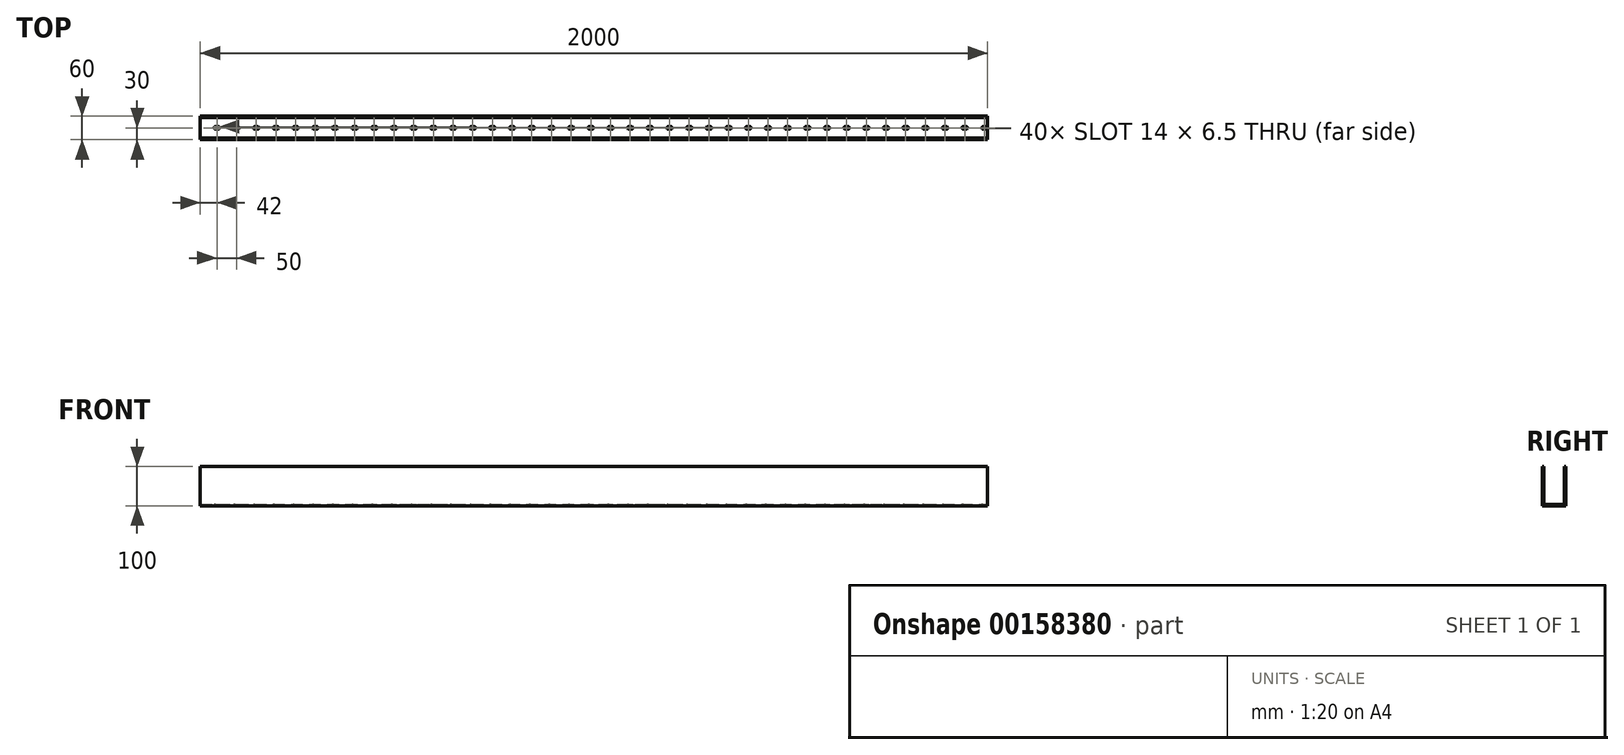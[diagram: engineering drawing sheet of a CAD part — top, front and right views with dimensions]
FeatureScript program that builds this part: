
annotation { "Feature Type Name" : "Feature", "Feature Type Description" : "" }
export const myFeature = defineFeature(function(context is Context, id is Id, definition is map)
    precondition{}
    {
        {
            var Q0;
            Q0=qCreatedBy(makeId("Top.planeOp"),FACE);
            var sketch = newSketch(context, id + "F0", { "sketchPlane" : qUnion([Q0])});
            skLineSegment(sketch, "E0.bottom", {"start": v(0, 0) * mm, "end": v(2000, 0) * mm});
            skLineSegment(sketch, "E0.top", {"start": v(0, 60) * mm, "end": v(2000, 60) * mm});
            skLineSegment(sketch, "E0.left", {"start": v(0, 0) * mm, "end": v(0, 60) * mm});
            skLineSegment(sketch, "E0.right", {"start": v(2000, 0) * mm, "end": v(2000, 60) * mm});
            skSolve(sketch);
        }
        {
            var Q0;
            Q0=qSketchRegion(id+"F0",true);
            extrude(context, id + "F1", {"entities" : qUnion([Q0]), "depth" : 100 * mm});
        }
        {
            var Q0;
            Q0=makeQuery(id+"F1.opExtrude","CAP_FACE",FACE,{"disambiguationData":[OSD([sQuery(id+"F0.wireOp",EDGE,"E0.bottom"),sQuery(id+"F0.wireOp",EDGE,"E0.top"),sQuery(id+"F0.wireOp",EDGE,"E0.left"),sQuery(id+"F0.wireOp",EDGE,"E0.right")])],"isStart":false});
            var sketch = newSketch(context, id + "F2", { "sketchPlane" : qUnion([Q0])});
            skLineSegment(sketch, "E1.bottom", {"start": v(0, 56) * mm, "end": v(2000, 56) * mm});
            skLineSegment(sketch, "E1.top", {"start": v(0, 4) * mm, "end": v(2000, 4) * mm});
            skLineSegment(sketch, "E1.left", {"start": v(0, 56) * mm, "end": v(0, 4) * mm});
            skLineSegment(sketch, "E1.right", {"start": v(2000, 56) * mm, "end": v(2000, 4) * mm});
            skSolve(sketch);
        }
        {
            var Q0;
            Q0=qSketchRegion(id+"F2",true);
            extrude(context, id + "F3", {"entities" : qUnion([Q0]), "operationType" : NewBodyOperationType.REMOVE, "oppositeDirection" : true, "depth" : (100 - 4) * mm});
        }
        {
            var Q0;
            Q0=makeQuery(id+"F3.boolean.opBoolean","COPY",FACE,{"derivedFrom":makeQuery(id+"F3.opExtrude","CAP_FACE",FACE,{"disambiguationData":[OSD([sQuery(id+"F2.wireOp",EDGE,"E1.bottom"),sQuery(id+"F2.wireOp",EDGE,"E1.top"),sQuery(id+"F2.wireOp",EDGE,"E1.left"),sQuery(id+"F2.wireOp",EDGE,"E1.right")])],"isStart":false})});
            var sketch = newSketch(context, id + "F4", { "sketchPlane" : qUnion([Q0])});
            skLineSegment(sketch, "E2", {"start": v(38.25, 30) * mm, "end": v(45.75, 30) * mm, "construction": true});
            skArc(sketch, "E3.0.startCap", {"start": v(38.25, 26.75) * mm, "mid": v(35, 30) * mm, "end": v(38.25, 33.25) * mm});
            skArc(sketch, "E3.0.endCap", {"start": v(45.75, 33.25) * mm, "mid": v(49, 30) * mm, "end": v(45.75, 26.75) * mm});
            skLineSegment(sketch, "E3.0.left", {"start": v(38.25, 33.25) * mm, "end": v(45.75, 33.25) * mm});
            skLineSegment(sketch, "E3.0.right", {"start": v(38.25, 26.75) * mm, "end": v(45.75, 26.75) * mm});
            skLineSegment(sketch, "E4.1.0.0", {"start": v(88.25, 26.75) * mm, "end": v(95.75, 26.75) * mm});
            skArc(sketch, "E4.1.0.1", {"start": v(88.25, 26.75) * mm, "mid": v(85, 30) * mm, "end": v(88.25, 33.25) * mm});
            skLineSegment(sketch, "E4.1.0.2", {"start": v(88.25, 33.25) * mm, "end": v(95.75, 33.25) * mm});
            skArc(sketch, "E4.1.0.3", {"start": v(95.75, 33.25) * mm, "mid": v(99, 30) * mm, "end": v(95.75, 26.75) * mm});
            skLineSegment(sketch, "E4.2.0.0", {"start": v(138.25, 26.75) * mm, "end": v(145.75, 26.75) * mm});
            skArc(sketch, "E4.2.0.1", {"start": v(138.25, 26.75) * mm, "mid": v(135, 30) * mm, "end": v(138.25, 33.25) * mm});
            skLineSegment(sketch, "E4.2.0.2", {"start": v(138.25, 33.25) * mm, "end": v(145.75, 33.25) * mm});
            skArc(sketch, "E4.2.0.3", {"start": v(145.75, 33.25) * mm, "mid": v(149, 30) * mm, "end": v(145.75, 26.75) * mm});
            skLineSegment(sketch, "E4.3.0.0", {"start": v(188.25, 26.75) * mm, "end": v(195.75, 26.75) * mm});
            skArc(sketch, "E4.3.0.1", {"start": v(188.25, 26.75) * mm, "mid": v(185, 30) * mm, "end": v(188.25, 33.25) * mm});
            skLineSegment(sketch, "E4.3.0.2", {"start": v(188.25, 33.25) * mm, "end": v(195.75, 33.25) * mm});
            skArc(sketch, "E4.3.0.3", {"start": v(195.75, 33.25) * mm, "mid": v(199, 30) * mm, "end": v(195.75, 26.75) * mm});
            skLineSegment(sketch, "E4.4.0.0", {"start": v(238.25, 26.75) * mm, "end": v(245.75, 26.75) * mm});
            skArc(sketch, "E4.4.0.1", {"start": v(238.25, 26.75) * mm, "mid": v(235, 30) * mm, "end": v(238.25, 33.25) * mm});
            skLineSegment(sketch, "E4.4.0.2", {"start": v(238.25, 33.25) * mm, "end": v(245.75, 33.25) * mm});
            skArc(sketch, "E4.4.0.3", {"start": v(245.75, 33.25) * mm, "mid": v(249, 30) * mm, "end": v(245.75, 26.75) * mm});
            skLineSegment(sketch, "E4.5.0.0", {"start": v(288.25, 26.75) * mm, "end": v(295.75, 26.75) * mm});
            skArc(sketch, "E4.5.0.1", {"start": v(288.25, 26.75) * mm, "mid": v(285, 30) * mm, "end": v(288.25, 33.25) * mm});
            skLineSegment(sketch, "E4.5.0.2", {"start": v(288.25, 33.25) * mm, "end": v(295.75, 33.25) * mm});
            skArc(sketch, "E4.5.0.3", {"start": v(295.75, 33.25) * mm, "mid": v(299, 30) * mm, "end": v(295.75, 26.75) * mm});
            skLineSegment(sketch, "E4.6.0.0", {"start": v(338.25, 26.75) * mm, "end": v(345.75, 26.75) * mm});
            skArc(sketch, "E4.6.0.1", {"start": v(338.25, 26.75) * mm, "mid": v(335, 30) * mm, "end": v(338.25, 33.25) * mm});
            skLineSegment(sketch, "E4.6.0.2", {"start": v(338.25, 33.25) * mm, "end": v(345.75, 33.25) * mm});
            skArc(sketch, "E4.6.0.3", {"start": v(345.75, 33.25) * mm, "mid": v(349, 30) * mm, "end": v(345.75, 26.75) * mm});
            skLineSegment(sketch, "E4.7.0.0", {"start": v(388.25, 26.75) * mm, "end": v(395.75, 26.75) * mm});
            skArc(sketch, "E4.7.0.1", {"start": v(388.25, 26.75) * mm, "mid": v(385, 30) * mm, "end": v(388.25, 33.25) * mm});
            skLineSegment(sketch, "E4.7.0.2", {"start": v(388.25, 33.25) * mm, "end": v(395.75, 33.25) * mm});
            skArc(sketch, "E4.7.0.3", {"start": v(395.75, 33.25) * mm, "mid": v(399, 30) * mm, "end": v(395.75, 26.75) * mm});
            skLineSegment(sketch, "E4.8.0.0", {"start": v(438.25, 26.75) * mm, "end": v(445.75, 26.75) * mm});
            skArc(sketch, "E4.8.0.1", {"start": v(438.25, 26.75) * mm, "mid": v(435, 30) * mm, "end": v(438.25, 33.25) * mm});
            skLineSegment(sketch, "E4.8.0.2", {"start": v(438.25, 33.25) * mm, "end": v(445.75, 33.25) * mm});
            skArc(sketch, "E4.8.0.3", {"start": v(445.75, 33.25) * mm, "mid": v(449, 30) * mm, "end": v(445.75, 26.75) * mm});
            skLineSegment(sketch, "E4.9.0.0", {"start": v(488.25, 26.75) * mm, "end": v(495.75, 26.75) * mm});
            skArc(sketch, "E4.9.0.1", {"start": v(488.25, 26.75) * mm, "mid": v(485, 30) * mm, "end": v(488.25, 33.25) * mm});
            skLineSegment(sketch, "E4.9.0.2", {"start": v(488.25, 33.25) * mm, "end": v(495.75, 33.25) * mm});
            skArc(sketch, "E4.9.0.3", {"start": v(495.75, 33.25) * mm, "mid": v(499, 30) * mm, "end": v(495.75, 26.75) * mm});
            skLineSegment(sketch, "E4.10.0.0", {"start": v(538.25, 26.75) * mm, "end": v(545.75, 26.75) * mm});
            skArc(sketch, "E4.10.0.1", {"start": v(538.25, 26.75) * mm, "mid": v(535, 30) * mm, "end": v(538.25, 33.25) * mm});
            skLineSegment(sketch, "E4.10.0.2", {"start": v(538.25, 33.25) * mm, "end": v(545.75, 33.25) * mm});
            skArc(sketch, "E4.10.0.3", {"start": v(545.75, 33.25) * mm, "mid": v(549, 30) * mm, "end": v(545.75, 26.75) * mm});
            skLineSegment(sketch, "E4.11.0.0", {"start": v(588.25, 26.75) * mm, "end": v(595.75, 26.75) * mm});
            skArc(sketch, "E4.11.0.1", {"start": v(588.25, 26.75) * mm, "mid": v(585, 30) * mm, "end": v(588.25, 33.25) * mm});
            skLineSegment(sketch, "E4.11.0.2", {"start": v(588.25, 33.25) * mm, "end": v(595.75, 33.25) * mm});
            skArc(sketch, "E4.11.0.3", {"start": v(595.75, 33.25) * mm, "mid": v(599, 30) * mm, "end": v(595.75, 26.75) * mm});
            skLineSegment(sketch, "E4.12.0.0", {"start": v(638.25, 26.75) * mm, "end": v(645.75, 26.75) * mm});
            skArc(sketch, "E4.12.0.1", {"start": v(638.25, 26.75) * mm, "mid": v(635, 30) * mm, "end": v(638.25, 33.25) * mm});
            skLineSegment(sketch, "E4.12.0.2", {"start": v(638.25, 33.25) * mm, "end": v(645.75, 33.25) * mm});
            skArc(sketch, "E4.12.0.3", {"start": v(645.75, 33.25) * mm, "mid": v(649, 30) * mm, "end": v(645.75, 26.75) * mm});
            skLineSegment(sketch, "E4.13.0.0", {"start": v(688.25, 26.75) * mm, "end": v(695.75, 26.75) * mm});
            skArc(sketch, "E4.13.0.1", {"start": v(688.25, 26.75) * mm, "mid": v(685, 30) * mm, "end": v(688.25, 33.25) * mm});
            skLineSegment(sketch, "E4.13.0.2", {"start": v(688.25, 33.25) * mm, "end": v(695.75, 33.25) * mm});
            skArc(sketch, "E4.13.0.3", {"start": v(695.75, 33.25) * mm, "mid": v(699, 30) * mm, "end": v(695.75, 26.75) * mm});
            skLineSegment(sketch, "E4.14.0.0", {"start": v(738.25, 26.75) * mm, "end": v(745.75, 26.75) * mm});
            skArc(sketch, "E4.14.0.1", {"start": v(738.25, 26.75) * mm, "mid": v(735, 30) * mm, "end": v(738.25, 33.25) * mm});
            skLineSegment(sketch, "E4.14.0.2", {"start": v(738.25, 33.25) * mm, "end": v(745.75, 33.25) * mm});
            skArc(sketch, "E4.14.0.3", {"start": v(745.75, 33.25) * mm, "mid": v(749, 30) * mm, "end": v(745.75, 26.75) * mm});
            skLineSegment(sketch, "E4.15.0.0", {"start": v(788.25, 26.75) * mm, "end": v(795.75, 26.75) * mm});
            skArc(sketch, "E4.15.0.1", {"start": v(788.25, 26.75) * mm, "mid": v(785, 30) * mm, "end": v(788.25, 33.25) * mm});
            skLineSegment(sketch, "E4.15.0.2", {"start": v(788.25, 33.25) * mm, "end": v(795.75, 33.25) * mm});
            skArc(sketch, "E4.15.0.3", {"start": v(795.75, 33.25) * mm, "mid": v(799, 30) * mm, "end": v(795.75, 26.75) * mm});
            skLineSegment(sketch, "E4.16.0.0", {"start": v(838.25, 26.75) * mm, "end": v(845.75, 26.75) * mm});
            skArc(sketch, "E4.16.0.1", {"start": v(838.25, 26.75) * mm, "mid": v(835, 30) * mm, "end": v(838.25, 33.25) * mm});
            skLineSegment(sketch, "E4.16.0.2", {"start": v(838.25, 33.25) * mm, "end": v(845.75, 33.25) * mm});
            skArc(sketch, "E4.16.0.3", {"start": v(845.75, 33.25) * mm, "mid": v(849, 30) * mm, "end": v(845.75, 26.75) * mm});
            skLineSegment(sketch, "E4.17.0.0", {"start": v(888.25, 26.75) * mm, "end": v(895.75, 26.75) * mm});
            skArc(sketch, "E4.17.0.1", {"start": v(888.25, 26.75) * mm, "mid": v(885, 30) * mm, "end": v(888.25, 33.25) * mm});
            skLineSegment(sketch, "E4.17.0.2", {"start": v(888.25, 33.25) * mm, "end": v(895.75, 33.25) * mm});
            skArc(sketch, "E4.17.0.3", {"start": v(895.75, 33.25) * mm, "mid": v(899, 30) * mm, "end": v(895.75, 26.75) * mm});
            skLineSegment(sketch, "E4.18.0.0", {"start": v(938.25, 26.75) * mm, "end": v(945.75, 26.75) * mm});
            skArc(sketch, "E4.18.0.1", {"start": v(938.25, 26.75) * mm, "mid": v(935, 30) * mm, "end": v(938.25, 33.25) * mm});
            skLineSegment(sketch, "E4.18.0.2", {"start": v(938.25, 33.25) * mm, "end": v(945.75, 33.25) * mm});
            skArc(sketch, "E4.18.0.3", {"start": v(945.75, 33.25) * mm, "mid": v(949, 30) * mm, "end": v(945.75, 26.75) * mm});
            skLineSegment(sketch, "E4.19.0.0", {"start": v(988.25, 26.75) * mm, "end": v(995.75, 26.75) * mm});
            skArc(sketch, "E4.19.0.1", {"start": v(988.25, 26.75) * mm, "mid": v(985, 30) * mm, "end": v(988.25, 33.25) * mm});
            skLineSegment(sketch, "E4.19.0.2", {"start": v(988.25, 33.25) * mm, "end": v(995.75, 33.25) * mm});
            skArc(sketch, "E4.19.0.3", {"start": v(995.75, 33.25) * mm, "mid": v(999, 30) * mm, "end": v(995.75, 26.75) * mm});
            skLineSegment(sketch, "E4.20.0.0", {"start": v(1038.25, 26.75) * mm, "end": v(1045.75, 26.75) * mm});
            skArc(sketch, "E4.20.0.1", {"start": v(1038.25, 26.75) * mm, "mid": v(1035, 30) * mm, "end": v(1038.25, 33.25) * mm});
            skLineSegment(sketch, "E4.20.0.2", {"start": v(1038.25, 33.25) * mm, "end": v(1045.75, 33.25) * mm});
            skArc(sketch, "E4.20.0.3", {"start": v(1045.75, 33.25) * mm, "mid": v(1049, 30) * mm, "end": v(1045.75, 26.75) * mm});
            skLineSegment(sketch, "E4.21.0.0", {"start": v(1088.25, 26.75) * mm, "end": v(1095.75, 26.75) * mm});
            skArc(sketch, "E4.21.0.1", {"start": v(1088.25, 26.75) * mm, "mid": v(1085, 30) * mm, "end": v(1088.25, 33.25) * mm});
            skLineSegment(sketch, "E4.21.0.2", {"start": v(1088.25, 33.25) * mm, "end": v(1095.75, 33.25) * mm});
            skArc(sketch, "E4.21.0.3", {"start": v(1095.75, 33.25) * mm, "mid": v(1099, 30) * mm, "end": v(1095.75, 26.75) * mm});
            skLineSegment(sketch, "E4.22.0.0", {"start": v(1138.25, 26.75) * mm, "end": v(1145.75, 26.75) * mm});
            skArc(sketch, "E4.22.0.1", {"start": v(1138.25, 26.75) * mm, "mid": v(1135, 30) * mm, "end": v(1138.25, 33.25) * mm});
            skLineSegment(sketch, "E4.22.0.2", {"start": v(1138.25, 33.25) * mm, "end": v(1145.75, 33.25) * mm});
            skArc(sketch, "E4.22.0.3", {"start": v(1145.75, 33.25) * mm, "mid": v(1149, 30) * mm, "end": v(1145.75, 26.75) * mm});
            skLineSegment(sketch, "E4.23.0.0", {"start": v(1188.25, 26.75) * mm, "end": v(1195.75, 26.75) * mm});
            skArc(sketch, "E4.23.0.1", {"start": v(1188.25, 26.75) * mm, "mid": v(1185, 30) * mm, "end": v(1188.25, 33.25) * mm});
            skLineSegment(sketch, "E4.23.0.2", {"start": v(1188.25, 33.25) * mm, "end": v(1195.75, 33.25) * mm});
            skArc(sketch, "E4.23.0.3", {"start": v(1195.75, 33.25) * mm, "mid": v(1199, 30) * mm, "end": v(1195.75, 26.75) * mm});
            skLineSegment(sketch, "E4.24.0.0", {"start": v(1238.25, 26.75) * mm, "end": v(1245.75, 26.75) * mm});
            skArc(sketch, "E4.24.0.1", {"start": v(1238.25, 26.75) * mm, "mid": v(1235, 30) * mm, "end": v(1238.25, 33.25) * mm});
            skLineSegment(sketch, "E4.24.0.2", {"start": v(1238.25, 33.25) * mm, "end": v(1245.75, 33.25) * mm});
            skArc(sketch, "E4.24.0.3", {"start": v(1245.75, 33.25) * mm, "mid": v(1249, 30) * mm, "end": v(1245.75, 26.75) * mm});
            skLineSegment(sketch, "E4.25.0.0", {"start": v(1288.25, 26.75) * mm, "end": v(1295.75, 26.75) * mm});
            skArc(sketch, "E4.25.0.1", {"start": v(1288.25, 26.75) * mm, "mid": v(1285, 30) * mm, "end": v(1288.25, 33.25) * mm});
            skLineSegment(sketch, "E4.25.0.2", {"start": v(1288.25, 33.25) * mm, "end": v(1295.75, 33.25) * mm});
            skArc(sketch, "E4.25.0.3", {"start": v(1295.75, 33.25) * mm, "mid": v(1299, 30) * mm, "end": v(1295.75, 26.75) * mm});
            skLineSegment(sketch, "E4.26.0.0", {"start": v(1338.25, 26.75) * mm, "end": v(1345.75, 26.75) * mm});
            skArc(sketch, "E4.26.0.1", {"start": v(1338.25, 26.75) * mm, "mid": v(1335, 30) * mm, "end": v(1338.25, 33.25) * mm});
            skLineSegment(sketch, "E4.26.0.2", {"start": v(1338.25, 33.25) * mm, "end": v(1345.75, 33.25) * mm});
            skArc(sketch, "E4.26.0.3", {"start": v(1345.75, 33.25) * mm, "mid": v(1349, 30) * mm, "end": v(1345.75, 26.75) * mm});
            skLineSegment(sketch, "E4.27.0.0", {"start": v(1388.25, 26.75) * mm, "end": v(1395.75, 26.75) * mm});
            skArc(sketch, "E4.27.0.1", {"start": v(1388.25, 26.75) * mm, "mid": v(1385, 30) * mm, "end": v(1388.25, 33.25) * mm});
            skLineSegment(sketch, "E4.27.0.2", {"start": v(1388.25, 33.25) * mm, "end": v(1395.75, 33.25) * mm});
            skArc(sketch, "E4.27.0.3", {"start": v(1395.75, 33.25) * mm, "mid": v(1399, 30) * mm, "end": v(1395.75, 26.75) * mm});
            skLineSegment(sketch, "E4.28.0.0", {"start": v(1438.25, 26.75) * mm, "end": v(1445.75, 26.75) * mm});
            skArc(sketch, "E4.28.0.1", {"start": v(1438.25, 26.75) * mm, "mid": v(1435, 30) * mm, "end": v(1438.25, 33.25) * mm});
            skLineSegment(sketch, "E4.28.0.2", {"start": v(1438.25, 33.25) * mm, "end": v(1445.75, 33.25) * mm});
            skArc(sketch, "E4.28.0.3", {"start": v(1445.75, 33.25) * mm, "mid": v(1449, 30) * mm, "end": v(1445.75, 26.75) * mm});
            skLineSegment(sketch, "E4.29.0.0", {"start": v(1488.25, 26.75) * mm, "end": v(1495.75, 26.75) * mm});
            skArc(sketch, "E4.29.0.1", {"start": v(1488.25, 26.75) * mm, "mid": v(1485, 30) * mm, "end": v(1488.25, 33.25) * mm});
            skLineSegment(sketch, "E4.29.0.2", {"start": v(1488.25, 33.25) * mm, "end": v(1495.75, 33.25) * mm});
            skArc(sketch, "E4.29.0.3", {"start": v(1495.75, 33.25) * mm, "mid": v(1499, 30) * mm, "end": v(1495.75, 26.75) * mm});
            skLineSegment(sketch, "E4.30.0.0", {"start": v(1538.25, 26.75) * mm, "end": v(1545.75, 26.75) * mm});
            skArc(sketch, "E4.30.0.1", {"start": v(1538.25, 26.75) * mm, "mid": v(1535, 30) * mm, "end": v(1538.25, 33.25) * mm});
            skLineSegment(sketch, "E4.30.0.2", {"start": v(1538.25, 33.25) * mm, "end": v(1545.75, 33.25) * mm});
            skArc(sketch, "E4.30.0.3", {"start": v(1545.75, 33.25) * mm, "mid": v(1549, 30) * mm, "end": v(1545.75, 26.75) * mm});
            skLineSegment(sketch, "E4.31.0.0", {"start": v(1588.25, 26.75) * mm, "end": v(1595.75, 26.75) * mm});
            skArc(sketch, "E4.31.0.1", {"start": v(1588.25, 26.75) * mm, "mid": v(1585, 30) * mm, "end": v(1588.25, 33.25) * mm});
            skLineSegment(sketch, "E4.31.0.2", {"start": v(1588.25, 33.25) * mm, "end": v(1595.75, 33.25) * mm});
            skArc(sketch, "E4.31.0.3", {"start": v(1595.75, 33.25) * mm, "mid": v(1599, 30) * mm, "end": v(1595.75, 26.75) * mm});
            skLineSegment(sketch, "E4.32.0.0", {"start": v(1638.25, 26.75) * mm, "end": v(1645.75, 26.75) * mm});
            skArc(sketch, "E4.32.0.1", {"start": v(1638.25, 26.75) * mm, "mid": v(1635, 30) * mm, "end": v(1638.25, 33.25) * mm});
            skLineSegment(sketch, "E4.32.0.2", {"start": v(1638.25, 33.25) * mm, "end": v(1645.75, 33.25) * mm});
            skArc(sketch, "E4.32.0.3", {"start": v(1645.75, 33.25) * mm, "mid": v(1649, 30) * mm, "end": v(1645.75, 26.75) * mm});
            skLineSegment(sketch, "E4.33.0.0", {"start": v(1688.25, 26.75) * mm, "end": v(1695.75, 26.75) * mm});
            skArc(sketch, "E4.33.0.1", {"start": v(1688.25, 26.75) * mm, "mid": v(1685, 30) * mm, "end": v(1688.25, 33.25) * mm});
            skLineSegment(sketch, "E4.33.0.2", {"start": v(1688.25, 33.25) * mm, "end": v(1695.75, 33.25) * mm});
            skArc(sketch, "E4.33.0.3", {"start": v(1695.75, 33.25) * mm, "mid": v(1699, 30) * mm, "end": v(1695.75, 26.75) * mm});
            skLineSegment(sketch, "E4.34.0.0", {"start": v(1738.25, 26.75) * mm, "end": v(1745.75, 26.75) * mm});
            skArc(sketch, "E4.34.0.1", {"start": v(1738.25, 26.75) * mm, "mid": v(1735, 30) * mm, "end": v(1738.25, 33.25) * mm});
            skLineSegment(sketch, "E4.34.0.2", {"start": v(1738.25, 33.25) * mm, "end": v(1745.75, 33.25) * mm});
            skArc(sketch, "E4.34.0.3", {"start": v(1745.75, 33.25) * mm, "mid": v(1749, 30) * mm, "end": v(1745.75, 26.75) * mm});
            skLineSegment(sketch, "E4.35.0.0", {"start": v(1788.25, 26.75) * mm, "end": v(1795.75, 26.75) * mm});
            skArc(sketch, "E4.35.0.1", {"start": v(1788.25, 26.75) * mm, "mid": v(1785, 30) * mm, "end": v(1788.25, 33.25) * mm});
            skLineSegment(sketch, "E4.35.0.2", {"start": v(1788.25, 33.25) * mm, "end": v(1795.75, 33.25) * mm});
            skArc(sketch, "E4.35.0.3", {"start": v(1795.75, 33.25) * mm, "mid": v(1799, 30) * mm, "end": v(1795.75, 26.75) * mm});
            skLineSegment(sketch, "E4.36.0.0", {"start": v(1838.25, 26.75) * mm, "end": v(1845.75, 26.75) * mm});
            skArc(sketch, "E4.36.0.1", {"start": v(1838.25, 26.75) * mm, "mid": v(1835, 30) * mm, "end": v(1838.25, 33.25) * mm});
            skLineSegment(sketch, "E4.36.0.2", {"start": v(1838.25, 33.25) * mm, "end": v(1845.75, 33.25) * mm});
            skArc(sketch, "E4.36.0.3", {"start": v(1845.75, 33.25) * mm, "mid": v(1849, 30) * mm, "end": v(1845.75, 26.75) * mm});
            skLineSegment(sketch, "E4.37.0.0", {"start": v(1888.25, 26.75) * mm, "end": v(1895.75, 26.75) * mm});
            skArc(sketch, "E4.37.0.1", {"start": v(1888.25, 26.75) * mm, "mid": v(1885, 30) * mm, "end": v(1888.25, 33.25) * mm});
            skLineSegment(sketch, "E4.37.0.2", {"start": v(1888.25, 33.25) * mm, "end": v(1895.75, 33.25) * mm});
            skArc(sketch, "E4.37.0.3", {"start": v(1895.75, 33.25) * mm, "mid": v(1899, 30) * mm, "end": v(1895.75, 26.75) * mm});
            skLineSegment(sketch, "E4.38.0.0", {"start": v(1938.25, 26.75) * mm, "end": v(1945.75, 26.75) * mm});
            skArc(sketch, "E4.38.0.1", {"start": v(1938.25, 26.75) * mm, "mid": v(1935, 30) * mm, "end": v(1938.25, 33.25) * mm});
            skLineSegment(sketch, "E4.38.0.2", {"start": v(1938.25, 33.25) * mm, "end": v(1945.75, 33.25) * mm});
            skArc(sketch, "E4.38.0.3", {"start": v(1945.75, 33.25) * mm, "mid": v(1949, 30) * mm, "end": v(1945.75, 26.75) * mm});
            skLineSegment(sketch, "E4.39.0.0", {"start": v(1988.25, 26.75) * mm, "end": v(1995.75, 26.75) * mm});
            skArc(sketch, "E4.39.0.1", {"start": v(1988.25, 26.75) * mm, "mid": v(1985, 30) * mm, "end": v(1988.25, 33.25) * mm});
            skLineSegment(sketch, "E4.39.0.2", {"start": v(1988.25, 33.25) * mm, "end": v(1995.75, 33.25) * mm});
            skArc(sketch, "E4.39.0.3", {"start": v(1995.75, 33.25) * mm, "mid": v(1999, 30) * mm, "end": v(1995.75, 26.75) * mm});
            skLineSegment(sketch, "E4.direction1", {"start": v(38.25, 26.75) * mm, "end": v(88.25, 26.75) * mm, "construction": true});
            skSolve(sketch);
        }
        {
            var Q0;
            Q0=qSketchRegion(id+"F4",true);
            extrude(context, id + "F5", {"entities" : qUnion([Q0]), "operationType" : NewBodyOperationType.REMOVE, "endBound" : BoundingType.THROUGH_ALL, "oppositeDirection" : true, "depth" : 25 * mm});
        }
    });
